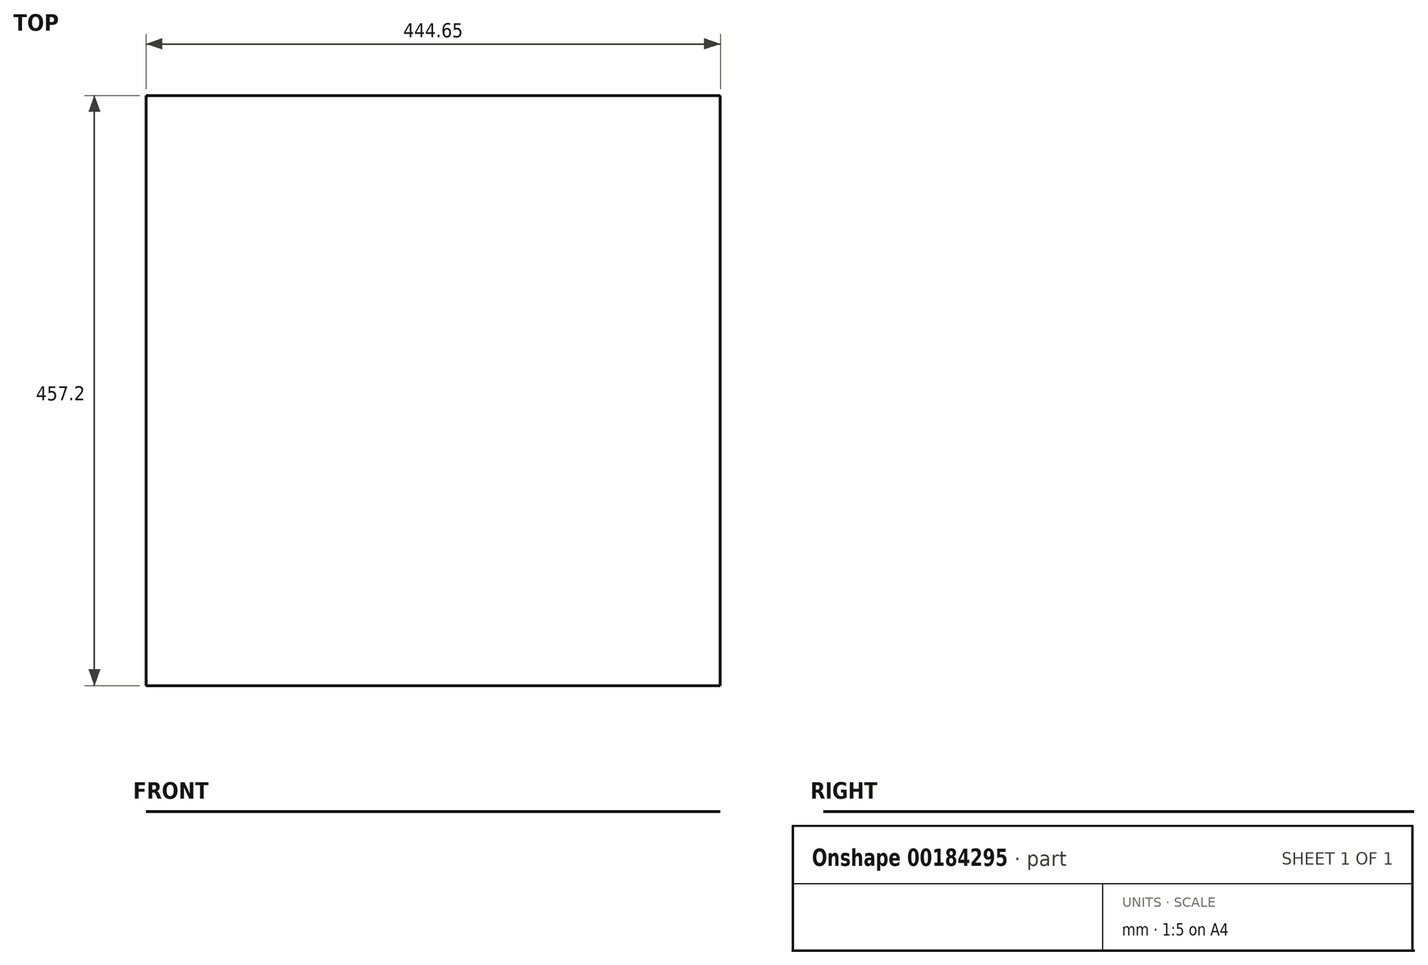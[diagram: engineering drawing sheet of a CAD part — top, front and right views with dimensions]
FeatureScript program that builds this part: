
annotation { "Feature Type Name" : "Feature", "Feature Type Description" : "" }
export const myFeature = defineFeature(function(context is Context, id is Id, definition is map)
    precondition{}
    {
        {
            var Q0;
            Q0=qCreatedBy(makeId("Top.planeOp"),FACE);
            var sketch = newSketch(context, id + "F0", { "sketchPlane" : qUnion([Q0])});
            skLineSegment(sketch, "E0.bottom", {"start": v(-185.6, 201.48) * mm, "end": v(259.05, 201.48) * mm});
            skLineSegment(sketch, "E0.top", {"start": v(-185.6, -255.72) * mm, "end": v(259.05, -255.72) * mm});
            skLineSegment(sketch, "E0.left", {"start": v(-185.6, 201.48) * mm, "end": v(-185.6, -255.72) * mm});
            skLineSegment(sketch, "E0.right", {"start": v(259.05, 201.48) * mm, "end": v(259.05, -255.72) * mm});
            skSolve(sketch);
        }
        {
            var Q0;
            Q0=makeQuery(id+"F0.imprint","IMPRINT",FACE,{"disambiguationData":[TD([[makeQuery(id+"F0.imprint","IMPRINT",EDGE,{"derivedFrom":sQuery(id+"F0.wireOp",EDGE,"E0.bottom")}),-1.0]])]});
            extrude(context, id + "F1", {"entities" : qUnion([Q0]), "depth" : 1 / 406.4 * mm});
        }
    });
